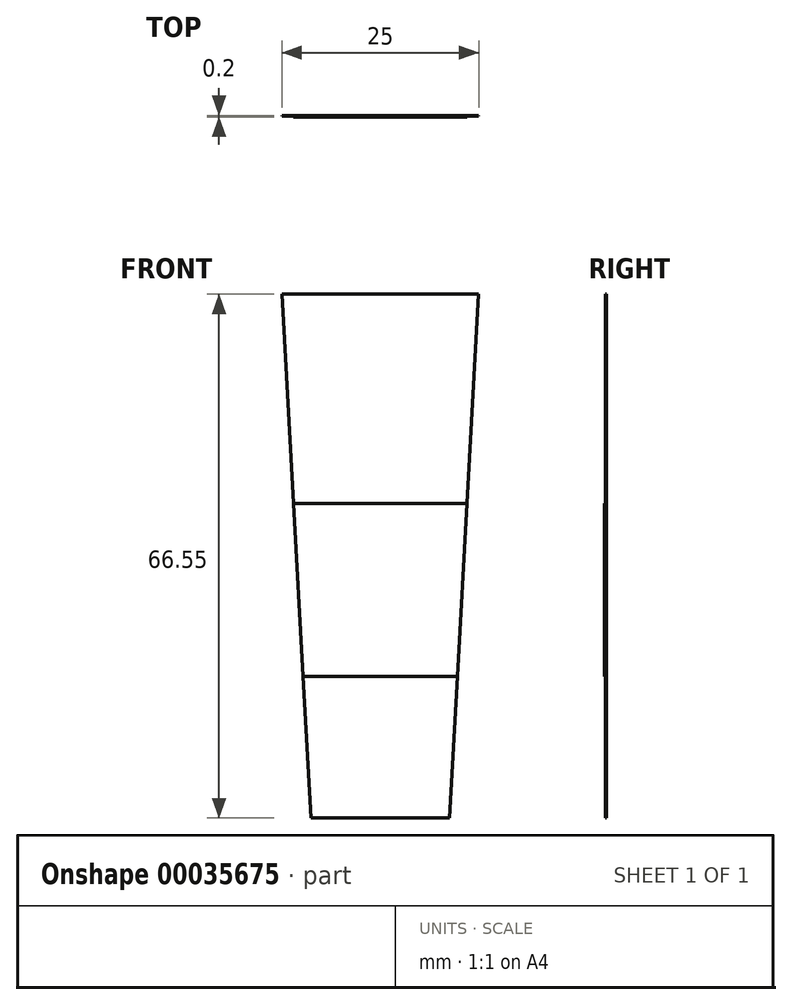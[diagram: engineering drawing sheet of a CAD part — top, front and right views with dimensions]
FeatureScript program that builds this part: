
annotation { "Feature Type Name" : "Feature", "Feature Type Description" : "" }
export const myFeature = defineFeature(function(context is Context, id is Id, definition is map)
    precondition{}
    {
        {
            var Q0;
            Q0=qCreatedBy(makeId("Front.planeOp"),FACE);
            var sketch = newSketch(context, id + "F0", { "sketchPlane" : qUnion([Q0])});
            skLineSegment(sketch, "E0", {"start": v(0, 0) * mm, "end": v(8.8, 0) * mm});
            skLineSegment(sketch, "E1", {"start": v(8.8, 0) * mm, "end": v(12.5, 66.55) * mm});
            skLineSegment(sketch, "E2", {"start": v(12.5, 66.55) * mm, "end": v(0, 66.55) * mm});
            skLineSegment(sketch, "E3", {"start": v(0, 39.93) * mm, "end": v(11.02, 39.93) * mm});
            skLineSegment(sketch, "E4", {"start": v(0, 66.55) * mm, "end": v(0, 0) * mm, "construction": true});
            skLineSegment(sketch, "E5", {"start": v(0, 18) * mm, "end": v(9.8, 18) * mm});
            skLineSegment(sketch, "E6.MirrorCS", {"start": v(-12.5, 66.55) * mm, "end": v(0, 66.55) * mm});
            skLineSegment(sketch, "E7.MirrorCS", {"start": v(-8.8, 0) * mm, "end": v(-12.5, 66.55) * mm});
            skLineSegment(sketch, "E8.MirrorCS", {"start": v(0, 39.93) * mm, "end": v(-11.02, 39.93) * mm});
            skLineSegment(sketch, "E9.MirrorCS", {"start": v(0, 18) * mm, "end": v(-9.8, 18) * mm});
            skLineSegment(sketch, "E10.MirrorCS", {"start": v(0, 0) * mm, "end": v(-8.8, 0) * mm});
            skSolve(sketch);
        }
        {
            var Q0;
            {var subQ2=sQuery(id+"F0.wireOp",EDGE,"E3");Q0=makeQuery(id+"F0.imprint","IMPRINT",FACE,{"disambiguationData":[TD([[makeQuery(id+"F0.imprint","IMPRINT",EDGE,{"derivedFrom":subQ2}),-1.0]])]});}
            extrude(context, id + "F1", {"entities" : qUnion([Q0]), "depth" : 0.2 * mm});
        }
        {
            var Q0;
            {var subQ5=sQuery(id+"F0.wireOp",EDGE,"E2");Q0=makeQuery(id+"F0.imprint","IMPRINT",FACE,{"disambiguationData":[TD([[makeQuery(id+"F0.imprint","IMPRINT",EDGE,{"derivedFrom":subQ5}),1.0]])]});}
            var Q1;
            {var subQ1=sQuery(id+"F0.wireOp",EDGE,"E0");Q1=makeQuery(id+"F0.imprint","IMPRINT",FACE,{"disambiguationData":[TD([[makeQuery(id+"F0.imprint","IMPRINT",EDGE,{"derivedFrom":subQ1}),1.0]])]});}
            extrude(context, id + "F2", {"entities" : qUnion([Q0, Q1]), "operationType" : NewBodyOperationType.ADD, "depth" : 0.1 * mm});
        }
    });
